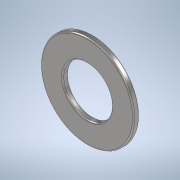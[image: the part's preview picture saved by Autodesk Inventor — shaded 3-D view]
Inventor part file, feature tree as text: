
AUTODESK INVENTOR PART (.ipt)
format: ipt  version: 2020 (Build 240168000, 168)  size: 135,168 bytes
history: native  units: mm
features: extrude x1, fillet x1, sketch x1
ambient origin geometry x8: Origin, YZ Plane, XZ Plane, XY Plane, X Axis, Y Axis, Z Axis, Center Point
bodies: Solid1 (feature_tree)
feature tree (3):
  extrude  "Extrusion1"  Depth=0.1mm
  fillet  "Fillet1"  Radius=0.5mm
  sketch  "Sketch1"  dims[d0=4.2mm d1=8.0mm d2=0.5mm d3=0.0mm d4=0.1mm]
